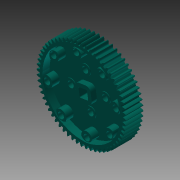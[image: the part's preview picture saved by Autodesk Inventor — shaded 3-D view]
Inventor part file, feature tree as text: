
AUTODESK INVENTOR PART (.ipt)
format: ipt  version: 2013 (Build 170138000, 138)  size: 706,560 bytes
history: native  units: in
note: dims shown in document units (in); Inventor stores cm internally (conversion verified against a paired STEP export)
features: extrude x9, plane x4, sketch x3, other x1
ambient origin geometry x8: Origin, YZ Plane, XZ Plane, XY Plane, X Axis, Y Axis, Z Axis, Center Point
bodies: Solid1 (feature_tree)
feature tree (17):
  sketch  "Sketch1"  dims[d0=0.5in d1=0.0in d2=-0.207in]
  extrude  "Extrusion1"  [1 undecoded]
  plane  "Work Plane1"
  plane  "Work Plane2"
  extrude  "Extrusion2"  Depth=0.5in TaperAngle=0.0deg
  extrude  "Extrusion3"  Depth=0.5in TaperAngle=0.0deg
  extrude  "Extrusion4"  Depth=0.019in
  plane  "Work Plane3"
  plane  "Work Plane4"
  extrude  "Extrusion5"  Depth=0.019in
  extrude  "Extrusion6"  Depth=0.5in TaperAngle=0.0deg
  extrude  "Extrusion7"  Depth=0.5in TaperAngle=0.0deg
  extrude  "Extrusion8"  Depth=0.1488in TaperAngle=0.0deg
  sketch  "Sketch2"  dims[d3=-0.207in d4=0.5in d5=0.0in]
  sketch  "Sketch3"  dims[d6=0.25in d7=0.0in d8=0.5in d9=0.0in d10=0.019in d11=0.019in d12=0.5in d13=0.0in d14=0.5in d15=0.0in d16=0.1488in d17=0.2354in d18=0.0in d19=0.0in d20=0.1488in d21=0.0in d22=0.1637in d23=0.0in d24=0.0in d25=0.0in]
  other  "Srf1"
  extrude  "ExtrusionSrf1"  Depth=0.1488in TaperAngle=0.0deg
note: 1 required parameter value undecoded (feature->parameter linkage not recoverable at this tier; creation-order binding heuristic only, values carry confidence <= 0.55)
